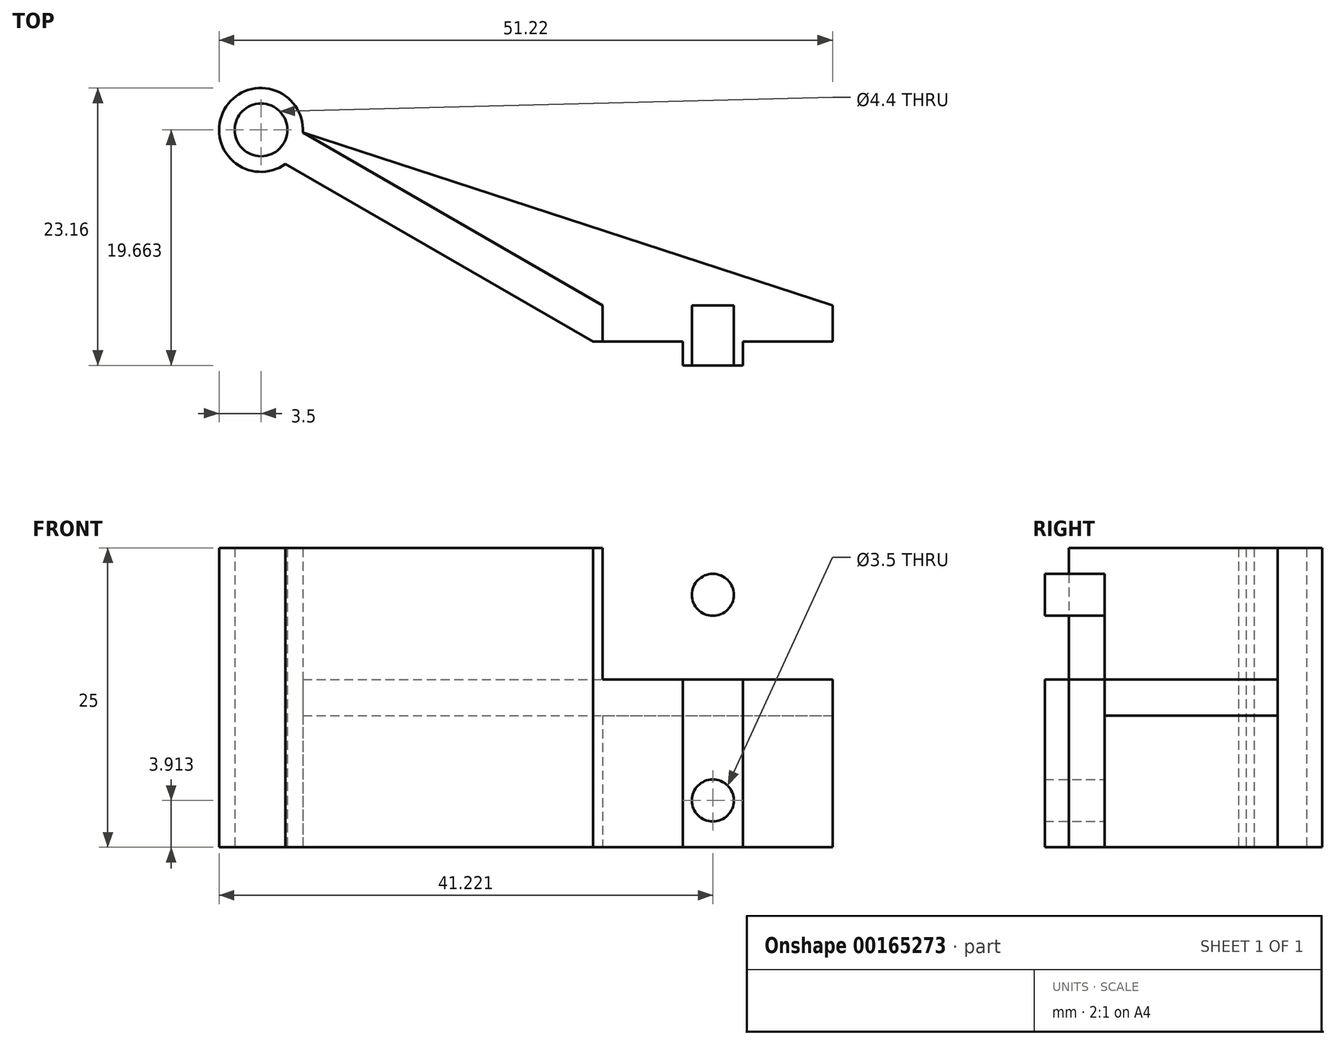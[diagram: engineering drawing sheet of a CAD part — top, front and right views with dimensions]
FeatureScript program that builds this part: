
annotation { "Feature Type Name" : "Feature", "Feature Type Description" : "" }
export const myFeature = defineFeature(function(context is Context, id is Id, definition is map)
    precondition{}
    {
        {
            var Q0;
            Q0=qCreatedBy(makeId("Top.planeOp"),FACE);
            var sketch = newSketch(context, id + "F0", { "sketchPlane" : qUnion([Q0])});
            skLineSegment(sketch, "E0.bottom", {"start": v(-23.66, 8.47) * mm, "end": v(-3.66, 8.47) * mm});
            skLineSegment(sketch, "E0.top", {"start": v(-23.66, 5.47) * mm, "end": v(-3.66, 5.47) * mm});
            skLineSegment(sketch, "E0.left", {"start": v(-23.66, 8.47) * mm, "end": v(-23.66, 5.47) * mm});
            skLineSegment(sketch, "E0.right", {"start": v(-3.66, 8.47) * mm, "end": v(-3.66, 5.47) * mm});
            skLineSegment(sketch, "E1.bottom", {"start": v(-48.14, 23.07) * mm, "end": v(-22.16, 8.07) * mm});
            skLineSegment(sketch, "E1.top", {"start": v(-49.64, 20.47) * mm, "end": v(-23.66, 5.47) * mm});
            skLineSegment(sketch, "E1.left", {"start": v(-48.14, 23.07) * mm, "end": v(-49.64, 20.47) * mm});
            skLineSegment(sketch, "E1.right", {"start": v(-22.16, 8.07) * mm, "end": v(-23.66, 5.47) * mm});
            skLineSegment(sketch, "E2.bottom", {"start": v(-16.16, 5.47) * mm, "end": v(-11.16, 5.47) * mm});
            skLineSegment(sketch, "E2.top", {"start": v(-16.16, 3.47) * mm, "end": v(-11.16, 3.47) * mm});
            skLineSegment(sketch, "E2.left", {"start": v(-16.16, 5.47) * mm, "end": v(-16.16, 3.47) * mm});
            skLineSegment(sketch, "E2.right", {"start": v(-11.16, 5.47) * mm, "end": v(-11.16, 3.47) * mm});
            skPoint(sketch, "E3", {"position": v(-13.66, 5.47) * mm});
            skCircle(sketch, "E4", {"center": v(-51.38, 23.13) * mm, "radius": 3.5 * mm});
            skCircle(sketch, "E5", {"center": v(-51.38, 23.13) * mm, "radius": 2.2 * mm});
            skSolve(sketch);
        }
        {
            var Q0;
            {var subQ5=sQuery(id+"F0.wireOp",EDGE,"E1.left");Q0=makeQuery(id+"F0.imprint","IMPRINT",FACE,{"disambiguationData":[TD([[makeQuery(id+"F0.imprint","IMPRINT",EDGE,{"derivedFrom":subQ5}),-1.0]])]});}
            var Q1;
            {var subQ3=sQuery(id+"F0.wireOp",EDGE,"E1.left");Q1=makeQuery(id+"F0.imprint","IMPRINT",FACE,{"disambiguationData":[TD([[makeQuery(id+"F0.imprint","IMPRINT",EDGE,{"derivedFrom":subQ3}),1.0]])]});}
            var Q2;
            {var subQ6=sQuery(id+"F0.wireOp",EDGE,"E0.left");Q2=makeQuery(id+"F0.imprint","IMPRINT",FACE,{"disambiguationData":[TD([[makeQuery(id+"F0.imprint","IMPRINT",EDGE,{"derivedFrom":subQ6}),-1.0]])]});}
            var Q3;
            Q3=makeQuery(id+"F0.imprint","IMPRINT",FACE,{"disambiguationData":[TD([[makeQuery(id+"F0.imprint","IMPRINT",EDGE,{"derivedFrom":sQuery(id+"F0.wireOp",EDGE,"E2.top")}),1.0]])]});
            var Q4;
            {var subQ4=sQuery(id+"F0.wireOp",EDGE,"E0.right");Q4=makeQuery(id+"F0.imprint","IMPRINT",FACE,{"disambiguationData":[TD([[makeQuery(id+"F0.imprint","IMPRINT",EDGE,{"derivedFrom":subQ4}),-1.0]])]});}
            var Q5;
            {var subQ3=sQuery(id+"F0.wireOp",EDGE,"E0.left");Q5=makeQuery(id+"F0.imprint","IMPRINT",FACE,{"disambiguationData":[TD([[makeQuery(id+"F0.imprint","IMPRINT",EDGE,{"derivedFrom":subQ3}),1.0]])]});}
            extrude(context, id + "F1", {"entities" : qUnion([Q0, Q1, Q2, Q3, Q4, Q5]), "depth" : 25 * mm, "offsetDistance" : 25 * mm});
        }
        {
            var Q0;
            Q0=qCreatedBy(makeId("Top.planeOp"),FACE);
            cPlane(context, id + "F2", {"entities" : qUnion([Q0]), "cplaneType" : CPlaneType.OFFSET, "offset" : 12.5 * mm, "width" : 150 * mm, "height" : 150 * mm});
        }
        {
            var Q0;
            Q0=qCreatedBy(id+"F2.planeOp",FACE);
            var sketch = newSketch(context, id + "F3", { "sketchPlane" : qUnion([Q0])});
            skLineSegment(sketch, "E6.0", {"start": v(-47.89, 22.92) * mm, "end": v(-22.86, 8.47) * mm});
            skLineSegment(sketch, "E6.1", {"start": v(-22.86, 8.47) * mm, "end": v(-3.66, 8.47) * mm});
            skLineSegment(sketch, "E7", {"start": v(-47.89, 22.92) * mm, "end": v(-3.66, 8.47) * mm});
            skSolve(sketch);
        }
        {
            var Q0;
            Q0=makeQuery(id+"F3.imprint","IMPRINT",FACE,{"disambiguationData":[TD([[makeQuery(id+"F3.imprint","IMPRINT",EDGE,{"derivedFrom":sQuery(id+"F3.wireOp",EDGE,"E6.0")}),1.0]])]});
            extrude(context, id + "F4", {"entities" : qUnion([Q0]), "operationType" : NewBodyOperationType.ADD, "depth" : 1.5 * mm, "offsetDistance" : 25 * mm, "hasSecondDirection" : true, "secondDirectionOppositeDirection" : true, "secondDirectionDepth" : 1.5 * mm});
        }
        {
            var Q0;
            {var subQ0=sQuery(id+"F3.wireOp",EDGE,"E7");var subQ3=sQuery(id+"F0.wireOp",EDGE,"E0.bottom");Q0=makeQuery(id+"F4.boolean.opBoolean","SPLIT",FACE,{"disambiguationData":[TD([makeQuery(id+"F4.opExtrude","CAP_FACE",FACE,{"disambiguationData":[OSD([sQuery(id+"F3.wireOp",EDGE,"E6.0"),sQuery(id+"F3.wireOp",EDGE,"E6.1"),subQ0])],"isStart":false})])],"derivedFrom":makeQuery(id+"F1.opExtrude","SWEPT_FACE",FACE,{"disambiguationData":[OSD([subQ3])]})});}
            var sketch = newSketch(context, id + "F5", { "sketchPlane" : qUnion([Q0])});
            skCircle(sketch, "E8", {"center": v(13.66, 3.91) * mm, "radius": 1.75 * mm});
            skCircle(sketch, "E9.MirrorC", {"center": v(13.66, 21.09) * mm, "radius": 1.75 * mm});
            skPoint(sketch, "E10.0", {"position": v(13.66, 25) * mm});
            skSolve(sketch);
        }
        {
            var Q0;
            Q0=makeQuery(id+"F5.imprint","IMPRINT",FACE,{"disambiguationData":[TD([[makeQuery(id+"F5.imprint","IMPRINT",EDGE,{"derivedFrom":sQuery(id+"F5.wireOp",EDGE,"E8")}),1.0]])]});
            var Q1;
            Q1=makeQuery(id+"F5.imprint","IMPRINT",FACE,{"disambiguationData":[TD([[makeQuery(id+"F5.imprint","IMPRINT",EDGE,{"derivedFrom":sQuery(id+"F5.wireOp",EDGE,"E9.MirrorC")}),-1.0]])]});
            extrude(context, id + "F6", {"entities" : qUnion([Q0, Q1]), "operationType" : NewBodyOperationType.REMOVE, "oppositeDirection" : true, "depth" : 25 * mm, "offsetDistance" : 25 * mm});
        }
    });
